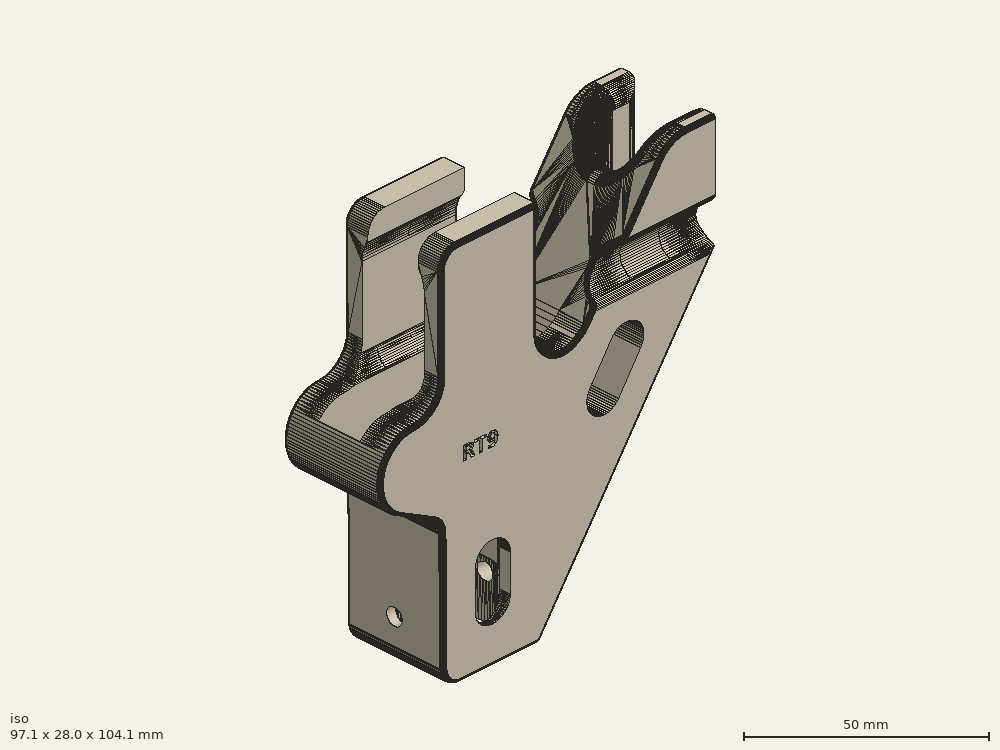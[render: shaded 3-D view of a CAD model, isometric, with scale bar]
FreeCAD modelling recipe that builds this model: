
FCSTD DOCUMENT  (FreeCAD 0.21RUnknown)
Label: poussey_clip
License: All rights reserved
LicenseURL: https://en.wikipedia.org/wiki/All_rights_reserved
objects: Part::Extrusion×8, Sketcher::SketchObject×6, Part::Cut×6, Part::Box×2, Part::MultiFuse×2, Part::Part2DObjectPython×2, Part::Feature×1, Part::Mirroring×1
note: 28 computed .brp shape members not serialized (recipe doc carries the construction recipe); baked Part::Feature solids carry a one-line shape summary decoded from their .brp

FEATURE [Part::Feature] poussey_clip_v008_solid  label="poussey_clip_v008 (Solid)"
  Placement = pos=(6,0,0) rot=(0,0,1;0rad)
  shape: bbox 97.06 x 28 x 104.1 mm, 23275 faces (baked)
FEATURE [Part::Box] Box  label="Cube"
  AttacherType = Attacher::AttachEngine3D
  Height = 10
  Length = 15
  Placement = pos=(30,0,5) rot=(0,0,1;0rad)
  Width = 5
FEATURE [Part::Box] Box001  label="Cube001"
  AttacherType = Attacher::AttachEngine3D
  Height = 10
  Length = 15
  Placement = pos=(30,23,5) rot=(0,0,1;0rad)
  Width = 5
FEATURE [Sketcher::SketchObject] Sketch001
  FullyConstrained = true
  MapMode = 5
  Placement = pos=(23.7725,0,0.14462) rot=(0.57891,-0.57891,-0.574218;2.0991rad)
  Support = -> [poussey_clip_v008_solid]
  sketch-geometry (4):
    g0: LineSegment StartX=-27.0261 StartY=-40.5361 StartZ=0 EndX=-0.999676 EndY=-40.5361 EndZ=0
    g1: LineSegment StartX=-0.999676 StartY=-40.5361 StartZ=0 EndX=-0.999676 EndY=-8.50434 EndZ=0
    g2: LineSegment StartX=-0.999676 StartY=-8.50434 StartZ=0 EndX=-27.0261 EndY=-8.50434 EndZ=0
    g3: LineSegment StartX=-27.0261 StartY=-8.50434 StartZ=0 EndX=-27.0261 EndY=-40.5361 EndZ=0
  constraints (10):
    c: Coincident(g0,g1)
    c: Coincident(g1,g2)
    c: Coincident(g2,g3)
    c: Coincident(g3,g0)
    c: Horizontal(g0)
    c: Horizontal(g2)
    c: Vertical(g1)
    c: Vertical(g3)
    c: Block(g1)
    c: Block(g2)
FEATURE [Part::Extrusion] Extrude
  Base = -> Sketch001
  Dir = (-1,0,0)
  DirMode = 0
  FaceMakerClass = Part::FaceMakerBullseye
  LengthFwd = 10
  LengthRev = 0
  Solid = true
  Symmetric = false
FEATURE [Sketcher::SketchObject] Sketch
  FullyConstrained = true
  MapMode = 5
  Placement = pos=(56.2,0,0) rot=(0.57735,0.57735,0.57735;2.0944rad)
  sketch-geometry (4):
    g0: LineSegment StartX=9.64311 StartY=-20.3721 StartZ=0 EndX=18.052 EndY=-20.3721 EndZ=0
    g1: LineSegment StartX=18.052 StartY=-20.3721 StartZ=0 EndX=18.052 EndY=-29.8321 EndZ=0
    g2: LineSegment StartX=18.052 StartY=-29.8321 StartZ=0 EndX=9.64311 EndY=-29.8321 EndZ=0
    g3: LineSegment StartX=9.64311 StartY=-29.8321 StartZ=0 EndX=9.64311 EndY=-20.3721 EndZ=0
  constraints (10):
    c: Coincident(g0,g1)
    c: Coincident(g1,g2)
    c: Coincident(g2,g3)
    c: Coincident(g3,g0)
    c: Horizontal(g0)
    c: Horizontal(g2)
    c: Vertical(g1)
    c: Vertical(g3)
    c: Block(g3)
    c: Block(g0)
FEATURE [Part::Extrusion] Extrude001
  Base = -> Sketch
  Dir = (1,0,0)
  DirMode = 2
  FaceMakerClass = Part::FaceMakerBullseye
  LengthFwd = 34
  LengthRev = 2
  Reversed = true
  Solid = true
  Symmetric = false
FEATURE [Part::MultiFuse] Fusion
  Refine = true
  Shapes = -> [poussey_clip_v008_solid,Box,Box001,Extrude001]
FEATURE [Part::Cut] Cut
  Base = -> Fusion
  Tool = -> Extrude
FEATURE [Sketcher::SketchObject] Sketch002
  FullyConstrained = true
  MapMode = 5
  Placement = pos=(56.2,0,0) rot=(0.57735,0.57735,0.57735;2.0944rad)
  sketch-geometry (6):
    g0: LineSegment StartX=22.7297 StartY=-25.1552 StartZ=0 EndX=22.7297 EndY=-45.6094 EndZ=0
    g1: LineSegment StartX=22.7297 StartY=-45.6094 StartZ=0 EndX=5.08629 EndY=-45.6094 EndZ=0
    g2: LineSegment StartX=5.08629 StartY=-45.6094 StartZ=0 EndX=5.08629 EndY=-25.1603 EndZ=0
    g3: LineSegment StartX=8.42624 StartY=-18.3823 StartZ=0 EndX=19.3794 EndY=-18.3823 EndZ=0
    g4: LineSegment StartX=19.3794 StartY=-18.3823 StartZ=0 EndX=22.7297 EndY=-25.1552 EndZ=0
    g5: LineSegment StartX=8.42624 StartY=-18.3823 StartZ=0 EndX=5.08629 EndY=-25.1603 EndZ=0
  constraints (15):
    c: Coincident(g0,g1)
    c: Coincident(g1,g2)
    c: Horizontal(g1)
    c: Vertical(g0)
    c: Vertical(g2)
    c: Horizontal(g3)
    c: Block(g2)
    c: Block(g1)
    c: Block(g0)
    c: Coincident(g4,g3)
    c: Coincident(g4,g0)
    c: Coincident(g5,g3)
    c: Coincident(g5,g2)
    c: Equal(g5,g4)
    c: Block(g5)
FEATURE [Part::Extrusion] Extrude002
  Base = -> Sketch002
  Dir = (1,0,0)
  DirMode = 2
  FaceMakerClass = Part::FaceMakerBullseye
  LengthFwd = 10
  LengthRev = 0
  Solid = true
  Symmetric = false
FEATURE [Part::Cut] Cut001
  Base = -> Cut
  Tool = -> Extrude002
FEATURE [Sketcher::SketchObject] Sketch003
  FullyConstrained = true
  MapMode = 5
  Placement = pos=(0,0,-29.8321) rot=(1,0,0;3.14159rad)
  Support = -> [Cut001]
  sketch-geometry (1):
    g0: Circle CenterX=38.3283 CenterY=-13.9463 CenterZ=0 NormalX=0 NormalY=0 NormalZ=1 AngleXU=0 Radius=11.9896
  constraints (1):
    c: Block(g0)
FEATURE [Part::Extrusion] Extrude003
  Base = -> Sketch003
  Dir = (0,0,-1)
  DirMode = 2
  FaceMakerClass = Part::FaceMakerBullseye
  LengthFwd = 10
  LengthRev = 1
  Reversed = true
  Solid = true
  Symmetric = false
FEATURE [Part::Cut] Cut002
  Base = -> Cut001
  Refine = true
  Tool = -> Extrude003
FEATURE [Sketcher::SketchObject] Sketch004
  FullyConstrained = true
  MapMode = 5
  Placement = pos=(56.2,1.08e-14,1.636e-13) rot=(0.57735,0.57735,0.57735;2.0944rad)
  Support = -> [Cut002]
  sketch-geometry (3):
    g0: Circle CenterX=14 CenterY=-33.3662 CenterZ=0 NormalX=0 NormalY=0 NormalZ=1 AngleXU=0 Radius=2.25
    g1: GeomPoint X=15.1201 Y=-45.3662 Z=0
    g2: GeomPoint X=0 Y=-34.2474 Z=0
  constraints (7):
    c: Diameter(g0) = 4.5
    c: DistanceY(g1,g0) = 12
    c: DistanceX(g2,g0) = 14
    c: DistanceX(g2) = 0
    c: DistanceY(g2) = -34.2474
    c: DistanceX(g1) = 15.1201
    c: DistanceY(g1) = -45.3662
FEATURE [Part::Extrusion] Extrude004  label="mount hole"
  Base = -> Sketch004
  Dir = (1,2e-16,2.9e-15)
  DirMode = 2
  FaceMakerClass = Part::FaceMakerBullseye
  LengthFwd = 50
  LengthRev = 10
  Reversed = true
  Solid = true
  Symmetric = false
FEATURE [Sketcher::SketchObject] Sketch005
  FullyConstrained = true
  MapMode = 5
  Placement = pos=(23.7721,0,0.193492) rot=(0.57891,-0.57891,-0.574217;2.0991rad)
  Support = -> [Cut002]
  sketch-geometry (4):
    g0: LineSegment StartX=-27.0063 StartY=-8.58159 StartZ=0 EndX=-0.988854 EndY=-8.58159 EndZ=0
    g1: LineSegment StartX=-0.988854 StartY=-8.58159 StartZ=0 EndX=-0.988854 EndY=-40.5713 EndZ=0
    g2: LineSegment StartX=-0.988854 StartY=-40.5713 StartZ=0 EndX=-27.0063 EndY=-40.5713 EndZ=0
    g3: LineSegment StartX=-27.0063 StartY=-40.5713 StartZ=0 EndX=-27.0063 EndY=-8.58159 EndZ=0
  constraints (10):
    c: Coincident(g0,g1)
    c: Coincident(g1,g2)
    c: Coincident(g2,g3)
    c: Coincident(g3,g0)
    c: Horizontal(g0)
    c: Horizontal(g2)
    c: Vertical(g1)
    c: Vertical(g3)
    c: Block(g0)
    c: Block(g1)
FEATURE [Part::Extrusion] Extrude005
  Base = -> Sketch005
  Dir = (-0.999967,0,-0.00813922)
  DirMode = 2
  FaceMakerClass = Part::FaceMakerBullseye
  LengthFwd = 0.1
  LengthRev = 2
  Solid = true
  Symmetric = false
FEATURE [Part::MultiFuse] Fusion001  label="shape withput mount hole"
  Refine = true
  Shapes = -> [Extrude005,Cut002]
FEATURE [Part::Cut] Cut003
  Base = -> Fusion001
  Tool = -> Extrude004
FEATURE [Part::Part2DObjectPython] ShapeString  # Draft 2D object (typed FeaturePython)
  FontFile = /nix/var/nix/profiles/system/sw/share/X11/fonts/DejaVuSans-Bold.ttf
  MakeFace = true
  Placement = pos=(40.59,28,9.67) rot=(0,1,1;3.14159rad)
  Size = 4
  String = RT9
  Tracking = 0
FEATURE [Part::Extrusion] Extrude006  label="rt9_1"
  Base = -> ShapeString
  Dir = (1e-16,1,0)
  DirMode = 2
  FaceMakerClass = Part::FaceMakerBullseye
  LengthFwd = 0
  LengthRev = 1
  Placement = pos=(0,0,-3) rot=(0,0,1;0rad)
  Solid = false
  Symmetric = false
FEATURE [Part::Part2DObjectPython] ShapeString001  # Draft 2D object (typed FeaturePython)
  FontFile = /nix/var/nix/profiles/system/sw/share/X11/fonts/DejaVuSans-Bold.ttf
  MakeFace = true
  Placement = pos=(40.59,28,9.67) rot=(0,0.707107,0.707107;3.14159rad)
  Size = 4
  String = RT9
  Tracking = 0
FEATURE [Part::Extrusion] Extrude007
  Base = -> ShapeString001
  Dir = (0,1,-2e-16)
  DirMode = 2
  FaceMakerClass = Part::FaceMakerBullseye
  LengthFwd = 1
  LengthRev = 0
  Solid = false
  Symmetric = false
FEATURE [Part::Mirroring] Part__Mirroring  label="rt9_2"
  Base = (0,0,0)
  Normal = (1,0,0)
  Placement = pos=(70,-28,-3) rot=(0,0,1;0rad)
  Source = -> Extrude007
FEATURE [Part::Cut] Cut004
  Base = -> Cut003
  Tool = -> Extrude006
FEATURE [Part::Cut] Cut005
  Base = -> Cut004
  Refine = true
  Tool = -> Part__Mirroring
